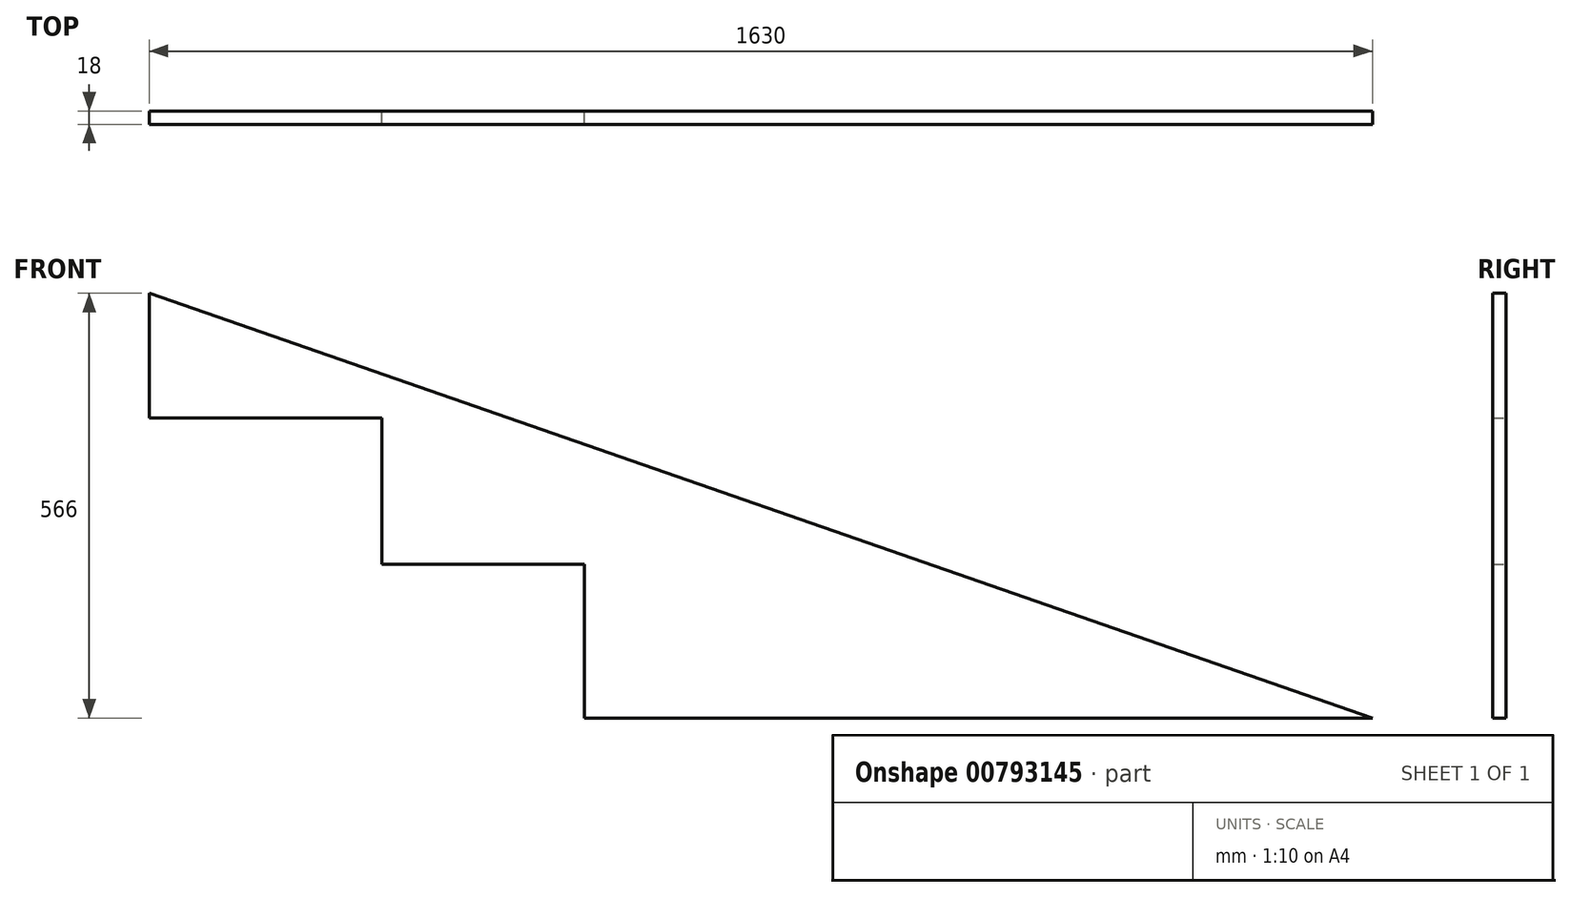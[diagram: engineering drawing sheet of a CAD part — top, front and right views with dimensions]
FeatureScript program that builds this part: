
annotation { "Feature Type Name" : "Feature", "Feature Type Description" : "" }
export const myFeature = defineFeature(function(context is Context, id is Id, definition is map)
    precondition{}
    {
        {
            var Q0;
            Q0=qCreatedBy(makeId("Front.planeOp"),FACE);
            var sketch = newSketch(context, id + "F0", { "sketchPlane" : qUnion([Q0])});
            skLineSegment(sketch, "E0", {"start": v(-62.58, 117) * mm, "end": v(-62.58, -49) * mm});
            skLineSegment(sketch, "E1", {"start": v(-62.58, -49) * mm, "end": v(247.42, -49) * mm});
            skLineSegment(sketch, "E2", {"start": v(247.42, -49) * mm, "end": v(247.42, -244) * mm});
            skLineSegment(sketch, "E3", {"start": v(247.42, -244) * mm, "end": v(517.42, -244) * mm});
            skLineSegment(sketch, "E4", {"start": v(517.42, -244) * mm, "end": v(517.42, -449) * mm});
            skLineSegment(sketch, "E5", {"start": v(517.42, -449) * mm, "end": v(1567.42, -449) * mm});
            skLineSegment(sketch, "E6", {"start": v(1567.42, -449) * mm, "end": v(-62.58, 117) * mm});
            skSolve(sketch);
        }
        {
            var Q0;
            Q0=makeQuery(id+"F0.imprint","IMPRINT",FACE,{"disambiguationData":[TD([[makeQuery(id+"F0.imprint","IMPRINT",EDGE,{"derivedFrom":sQuery(id+"F0.wireOp",EDGE,"E0")}),1.0]])]});
            extrude(context, id + "F1", {"entities" : qUnion([Q0]), "depth" : 18 * mm, "offsetDistance" : 25 * mm});
        }
    });
